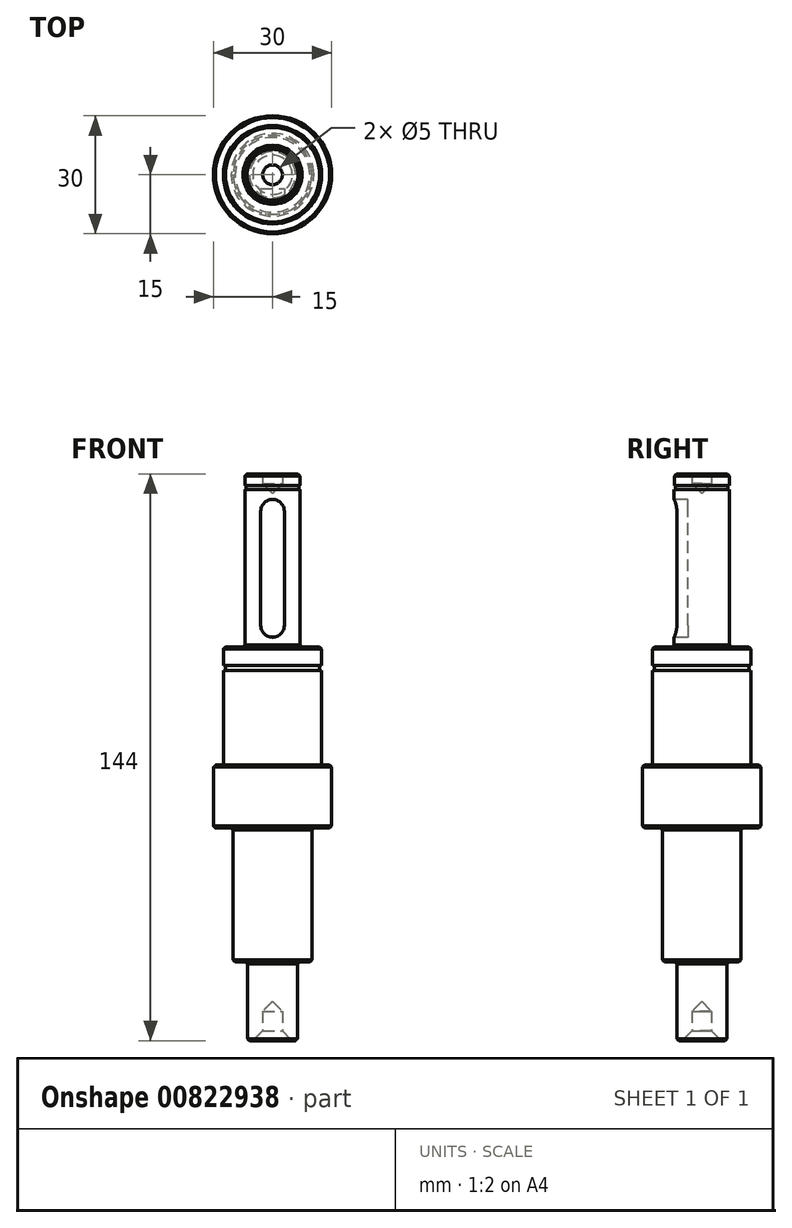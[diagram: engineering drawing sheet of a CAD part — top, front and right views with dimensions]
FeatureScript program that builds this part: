
annotation { "Feature Type Name" : "Feature", "Feature Type Description" : "" }
export const myFeature = defineFeature(function(context is Context, id is Id, definition is map)
    precondition{}
    {
        {
            var Q0;
            Q0=qCreatedBy(makeId("Front.planeOp"),FACE);
            var sketch = newSketch(context, id + "F0", { "sketchPlane" : qUnion([Q0])});
            skLineSegment(sketch, "E0", {"start": v(0, 0) * mm, "end": v(0, 15) * mm});
            skLineSegment(sketch, "E1", {"start": v(0, 15) * mm, "end": v(2.5, 17.5) * mm});
            skLineSegment(sketch, "E2", {"start": v(2.5, 17.5) * mm, "end": v(2.5, 20) * mm});
            skLineSegment(sketch, "E3", {"start": v(2.5, 20) * mm, "end": v(6.98, 20) * mm});
            skLineSegment(sketch, "E4", {"start": v(6.98, 20) * mm, "end": v(6.98, 17.1) * mm});
            skLineSegment(sketch, "E5", {"start": v(6.98, 17.1) * mm, "end": v(6.7, 17.1) * mm});
            skLineSegment(sketch, "E6", {"start": v(6.7, 17.1) * mm, "end": v(6.7, 16) * mm});
            skLineSegment(sketch, "E7", {"start": v(6.7, 16) * mm, "end": v(7, 16) * mm});
            skLineSegment(sketch, "E8", {"start": v(7, 16) * mm, "end": v(7, -24) * mm});
            skLineSegment(sketch, "E9", {"start": v(7, -24) * mm, "end": v(12.48, -24) * mm});
            skLineSegment(sketch, "E10", {"start": v(12.48, -24) * mm, "end": v(12.48, -28.7) * mm});
            skLineSegment(sketch, "E11", {"start": v(12.48, -28.7) * mm, "end": v(11.95, -28.7) * mm});
            skLineSegment(sketch, "E12", {"start": v(11.95, -28.7) * mm, "end": v(11.95, -30) * mm});
            skLineSegment(sketch, "E13", {"start": v(11.95, -30) * mm, "end": v(12.5, -30) * mm});
            skLineSegment(sketch, "E14", {"start": v(12.5, -30) * mm, "end": v(12.5, -54) * mm});
            skLineSegment(sketch, "E15", {"start": v(12.5, -54) * mm, "end": v(15, -54) * mm});
            skLineSegment(sketch, "E16", {"start": v(15, -54) * mm, "end": v(15, -70) * mm});
            skLineSegment(sketch, "E17", {"start": v(10, -104) * mm, "end": v(6.35, -104) * mm});
            skLineSegment(sketch, "E18", {"start": v(6.35, -104) * mm, "end": v(6.35, -124) * mm});
            skLineSegment(sketch, "E19", {"start": v(2.5, -121.5) * mm, "end": v(2.5, -116.5) * mm});
            skLineSegment(sketch, "E20", {"start": v(2.5, -116.5) * mm, "end": v(0, -114) * mm});
            skLineSegment(sketch, "E21", {"start": v(0, -114) * mm, "end": v(0, 0) * mm});
            skLineSegment(sketch, "E22", {"start": v(6.35, -124) * mm, "end": v(5, -124) * mm});
            skLineSegment(sketch, "E23", {"start": v(5, -124) * mm, "end": v(2.5, -121.5) * mm});
            skLineSegment(sketch, "E24", {"start": v(0, 15) * mm, "end": v(0, 95.93) * mm, "construction": true});
            skLineSegment(sketch, "E25", {"start": v(0, -104.42) * mm, "end": v(0, -114) * mm, "construction": true});
            skLineSegment(sketch, "E26", {"start": v(10, -104) * mm, "end": v(10, -70) * mm});
            skLineSegment(sketch, "E27", {"start": v(10, -70) * mm, "end": v(15, -70) * mm});
            skPoint(sketch, "E28.orphan", {"position": v(15, -104) * mm});
            skSolve(sketch);
        }
        {
            var Q0;
            Q0=qSketchRegion(id+"F0",true);
            var Q1;
            Q1=sQuery(id+"F0.wireOp",EDGE,"E24");
            revolve(context, id + "F1", {"surfaceOperationType" : NewSurfaceOperationType.NEW, "entities" : qUnion([Q0]), "axis" : qUnion([Q1]), "revolveType" : RevolveType.FULL});
        }
        {
            var Q0;
            Q0=makeQuery(id+"F1.opRevolve","SWEPT_EDGE",EDGE,{"disambiguationData":[OSD([sQuery(id+"F0.wireOp",EDGE,"E3"),sQuery(id+"F0.wireOp",EDGE,"E4")])]});
            var Q1;
            Q1=makeQuery(id+"F1.opRevolve","SWEPT_FACE",FACE,{"disambiguationData":[OSD([sQuery(id+"F0.wireOp",EDGE,"E9")])]});
            var Q2;
            Q2=makeQuery(id+"F1.opRevolve","SWEPT_FACE",FACE,{"disambiguationData":[OSD([sQuery(id+"F0.wireOp",EDGE,"E17")])]});
            var Q3;
            Q3=makeQuery(id+"F1.opRevolve","SWEPT_EDGE",EDGE,{"disambiguationData":[OSD([sQuery(id+"F0.wireOp",EDGE,"E18"),sQuery(id+"F0.wireOp",EDGE,"E22")])]});
            var Q4;
            Q4=makeQuery(id+"F1.opRevolve","SWEPT_EDGE",EDGE,{"disambiguationData":[OSD([sQuery(id+"F0.wireOp",EDGE,"E15"),sQuery(id+"F0.wireOp",EDGE,"E16")])]});
            var Q5;
            Q5=makeQuery(id+"F1.opRevolve","SWEPT_EDGE",EDGE,{"disambiguationData":[OSD([sQuery(id+"F0.wireOp",EDGE,"E26"),sQuery(id+"F0.wireOp",EDGE,"E27")])]});
            var Q6;
            Q6=makeQuery(id+"F1.opRevolve","SWEPT_EDGE",EDGE,{"disambiguationData":[OSD([sQuery(id+"F0.wireOp",EDGE,"E16"),sQuery(id+"F0.wireOp",EDGE,"E27")])]});
            chamfer(context, id + "F2", {"entities" : qUnion([Q0, Q1, Q2, Q3, Q4, Q5, Q6]), "width" : 0.5 * mm, "tangentPropagation" : true});
        }
        {
            var Q0;
            Q0=makeQuery(id+"F1.opRevolve","SWEPT_EDGE",EDGE,{"disambiguationData":[OSD([sQuery(id+"F0.wireOp",EDGE,"E14"),sQuery(id+"F0.wireOp",EDGE,"E15")])]});
            fillet(context, id + "F3", {"entities" : qUnion([Q0]), "radius" : 0.5 * mm, "tangentPropagation" : true, "allowEdgeOverflow" : false});
        }
        {
            var Q0;
            Q0=qCreatedBy(makeId("Front.planeOp"),FACE);
            cPlane(context, id + "F4", {"entities" : qUnion([Q0]), "cplaneType" : CPlaneType.OFFSET, "offset" : 7 * mm, "width" : 150 * mm, "height" : 150 * mm});
        }
        {
            var Q0;
            Q0=qCreatedBy(id+"F4.planeOp",FACE);
            var sketch = newSketch(context, id + "F5", { "sketchPlane" : qUnion([Q0])});
            skLineSegment(sketch, "E29", {"start": v(0, 0) * mm, "end": v(0, 10.5) * mm, "construction": true});
            skLineSegment(sketch, "E30", {"start": v(0, -18.5) * mm, "end": v(0, 0) * mm, "construction": true});
            skArc(sketch, "E31", {"start": v(3, 10.5) * mm, "mid": v(0, 13.5) * mm, "end": v(-3, 10.5) * mm});
            skArc(sketch, "E32", {"start": v(-3, -18.5) * mm, "mid": v(0, -21.5) * mm, "end": v(3, -18.5) * mm});
            skLineSegment(sketch, "E33.0", {"start": v(7, 16) * mm, "end": v(-7, 16) * mm, "construction": true});
            skLineSegment(sketch, "E33.1", {"start": v(-11.98, -24) * mm, "end": v(11.98, -24) * mm, "construction": true});
            skLineSegment(sketch, "E34", {"start": v(3, -18.5) * mm, "end": v(3, 10.5) * mm});
            skLineSegment(sketch, "E35", {"start": v(-3, 10.5) * mm, "end": v(-3, -18.5) * mm});
            skSolve(sketch);
        }
        {
            var Q0;
            Q0=qSketchRegion(id+"F5",true);
            extrude(context, id + "F6", {"entities" : qUnion([Q0]), "operationType" : NewBodyOperationType.REMOVE, "oppositeDirection" : true, "depth" : 3.5 * mm, "offsetDistance" : 25 * mm});
        }
    });
